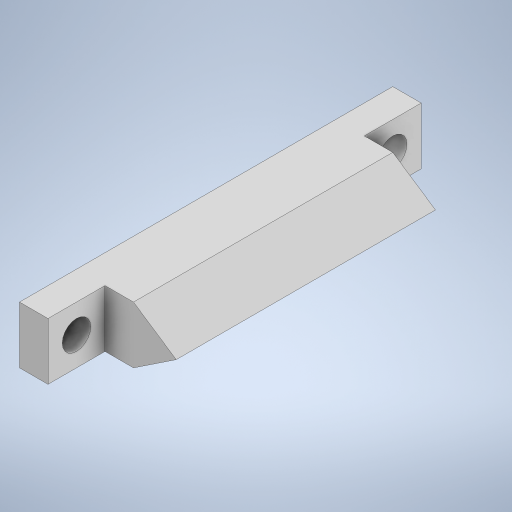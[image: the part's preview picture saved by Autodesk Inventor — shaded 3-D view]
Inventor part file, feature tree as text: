
AUTODESK INVENTOR PART (.ipt)
format: ipt  version: 2023 (Build 270158000, 158)  size: 262,144 bytes
history: native  units: mm
features: extrude x3, sketch x2
ambient origin geometry x8: Origin, YZ Plane, XZ Plane, XY Plane, X Axis, Y Axis, Z Axis, Center Point
bodies: Solid1 (feature_tree)
feature tree (5):
  sketch  "Sketch1"  dims[d0=10.0mm d1=0.0mm d2=5.0mm d3=0.0mm]
  extrude  "Extrusion1"  Depth=5.0mm TaperAngle=0.0deg
  extrude  "Extrusion2"  Depth=5.0mm TaperAngle=0.0deg
  extrude  "Extrusion3"  [1 undecoded]
  sketch  "Sketch2"  dims[d4=15.0mm d5=5.0mm d6=0.0mm]
note: 1 required parameter value undecoded (feature->parameter linkage not recoverable at this tier; creation-order binding heuristic only, values carry confidence <= 0.55)
